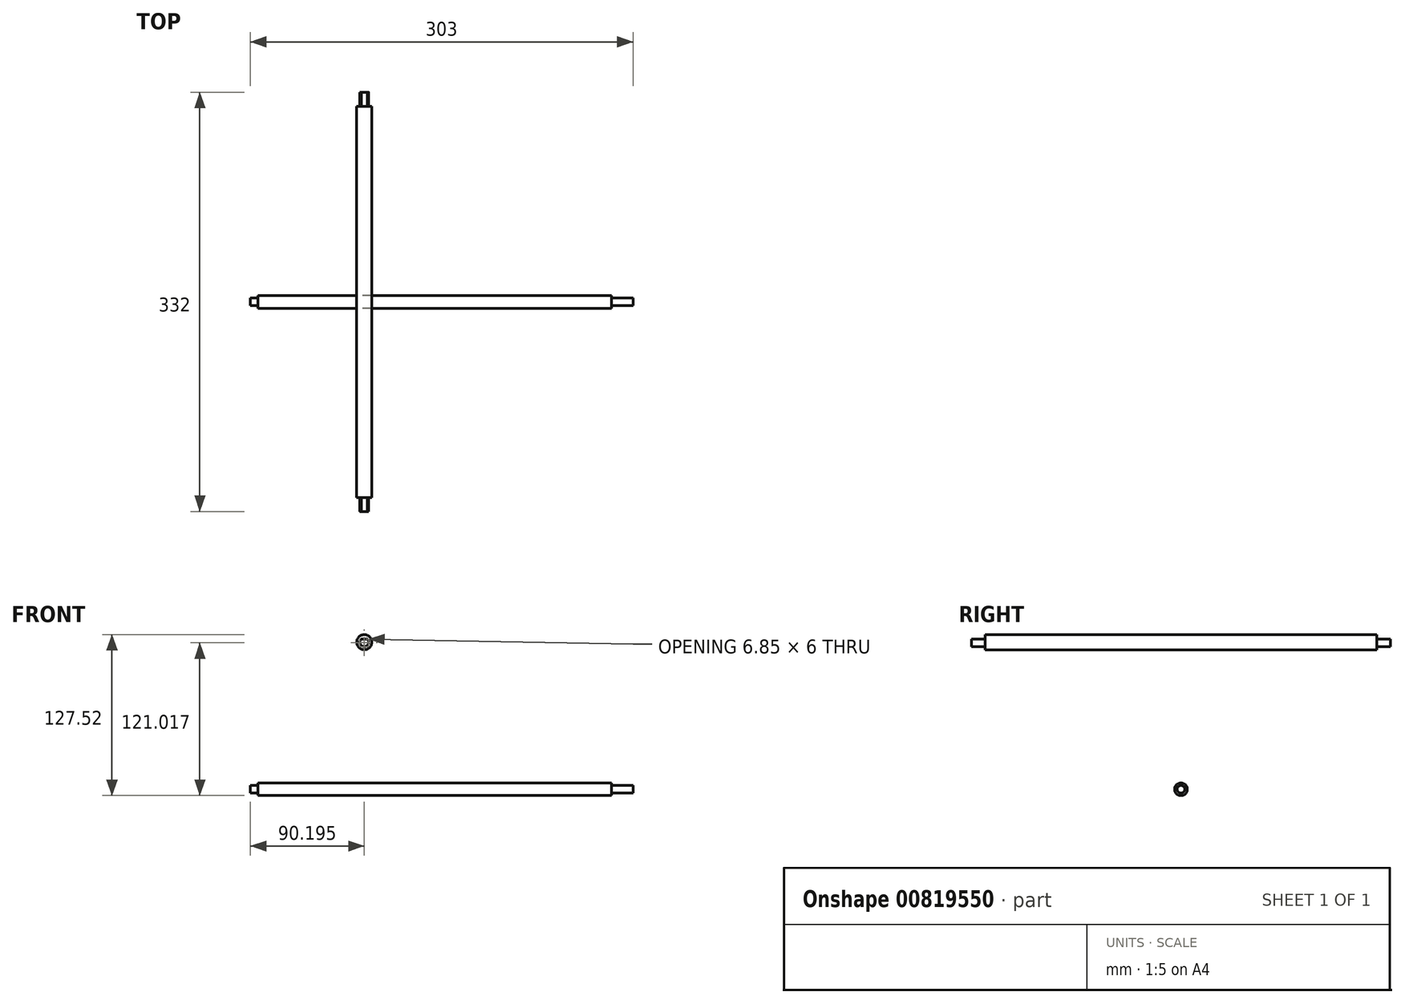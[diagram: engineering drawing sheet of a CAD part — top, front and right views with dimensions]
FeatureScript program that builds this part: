
annotation { "Feature Type Name" : "Feature", "Feature Type Description" : "" }
export const myFeature = defineFeature(function(context is Context, id is Id, definition is map)
    precondition{}
    {
        {
            var Q0;
            Q0=qCreatedBy(makeId("Right.planeOp"),FACE);
            var sketch = newSketch(context, id + "F0", { "sketchPlane" : qUnion([Q0])});
            skCircle(sketch, "E0", {"center": v(0, 0) * mm, "radius": 5 * mm});
            skSolve(sketch);
        }
        {
            var Q0;
            Q0=makeQuery(id+"F0.imprint","IMPRINT",FACE,{"disambiguationData":[TD([[makeQuery(id+"F0.imprint","IMPRINT",EDGE,{"derivedFrom":sQuery(id+"F0.wireOp",EDGE,"E0")}),1.0]])]});
            extrude(context, id + "F1", {"entities" : qUnion([Q0]), "endBound" : BoundingType.SYMMETRIC, "depth" : 280 * mm, "offsetDistance" : 25 * mm});
        }
        {
            var Q0;
            Q0=makeQuery(id+"F1.opExtrude","CAP_FACE",FACE,{"disambiguationData":[OSD([sQuery(id+"F0.wireOp",EDGE,"E0")])],"isStart":false});
            var sketch = newSketch(context, id + "F2", { "sketchPlane" : qUnion([Q0])});
            skCircle(sketch, "E1", {"center": v(0, 0) * mm, "radius": 3 * mm});
            skSolve(sketch);
        }
        {
            var Q0;
            Q0=makeQuery(id+"F2.imprint","IMPRINT",FACE,{"disambiguationData":[TD([[makeQuery(id+"F2.imprint","IMPRINT",EDGE,{"derivedFrom":sQuery(id+"F2.wireOp",EDGE,"E1")}),1.0]])]});
            extrude(context, id + "F3", {"entities" : qUnion([Q0]), "operationType" : NewBodyOperationType.ADD, "depth" : 17 * mm, "offsetDistance" : 25 * mm});
        }
        {
            var Q0;
            Q0=makeQuery(id+"F1.opExtrude","CAP_FACE",FACE,{"disambiguationData":[OSD([sQuery(id+"F0.wireOp",EDGE,"E0")])],"isStart":true});
            var sketch = newSketch(context, id + "F4", { "sketchPlane" : qUnion([Q0])});
            skCircle(sketch, "E2", {"center": v(0, 0) * mm, "radius": 3 * mm});
            skSolve(sketch);
        }
        {
            var Q0;
            Q0=makeQuery(id+"F4.imprint","IMPRINT",FACE,{"disambiguationData":[TD([[makeQuery(id+"F4.imprint","IMPRINT",EDGE,{"derivedFrom":sQuery(id+"F4.wireOp",EDGE,"E2")}),1.0]])]});
            extrude(context, id + "F5", {"entities" : qUnion([Q0]), "operationType" : NewBodyOperationType.ADD, "depth" : 6 * mm, "offsetDistance" : 25 * mm});
        }
        {
            var Q0;
            Q0=qCreatedBy(makeId("Front.planeOp"),FACE);
            var sketch = newSketch(context, id + "F6", { "sketchPlane" : qUnion([Q0])});
            skCircle(sketch, "E3", {"center": v(-55.8, 116.52) * mm, "radius": 6 * mm});
            skArc(sketch, "E4", {"start": v(-58.25, 119.02) * mm, "mid": v(-55.8, 113.02) * mm, "end": v(-53.36, 119.02) * mm});
            skLineSegment(sketch, "E5", {"start": v(-58.25, 119.02) * mm, "end": v(-53.36, 119.02) * mm});
            skSolve(sketch);
        }
        {
            var Q0;
            Q0=makeQuery(id+"F6.imprint","IMPRINT",FACE,{"disambiguationData":[TD([[makeQuery(id+"F6.imprint","IMPRINT",EDGE,{"derivedFrom":sQuery(id+"F6.wireOp",EDGE,"E4")}),1.0]])]});
            extrude(context, id + "F7", {"entities" : qUnion([Q0]), "endBound" : BoundingType.SYMMETRIC, "depth" : 332 * mm, "offsetDistance" : 25 * mm});
        }
        {
            var Q0;
            Q0=makeQuery(id+"F6.imprint","IMPRINT",FACE,{"disambiguationData":[TD([[makeQuery(id+"F6.imprint","IMPRINT",EDGE,{"derivedFrom":sQuery(id+"F6.wireOp",EDGE,"E3")}),1.0]])]});
            extrude(context, id + "F8", {"entities" : qUnion([Q0]), "operationType" : NewBodyOperationType.ADD, "endBound" : BoundingType.SYMMETRIC, "depth" : 310 * mm, "offsetDistance" : 25 * mm});
        }
    });
